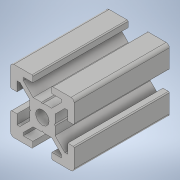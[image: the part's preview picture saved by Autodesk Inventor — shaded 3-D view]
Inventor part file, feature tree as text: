
AUTODESK INVENTOR PART (.ipt)
format: ipt  version: 2021.4 (Build 254397000, 397)  size: 193,536 bytes
history: native  units: mm
features: other x7, extrude x1, sketch x1
ambient origin geometry x8: Origin, YZ Plane, XZ Plane, XY Plane, X Axis, Y Axis, Z Axis, Center Point
bodies: Solid1 (feature_tree)
feature tree (9):
  extrude  "Extrusion1"  TaperAngle=0.0deg  [1 undecoded]
  other  "to_frame_XY"
  other  "to_frame_YZ"
  other  "to_frame_ZX"
  other  "to_frame_X"
  other  "to_frame_Y"
  other  "to_frame_Z"
  other  "to_frame_Center"
  sketch  "Sketch_5"  dims[d0=30.0mm d1=0.0mm d2=0.0mm]
note: 1 required parameter value undecoded (feature->parameter linkage not recoverable at this tier; creation-order binding heuristic only, values carry confidence <= 0.55)
